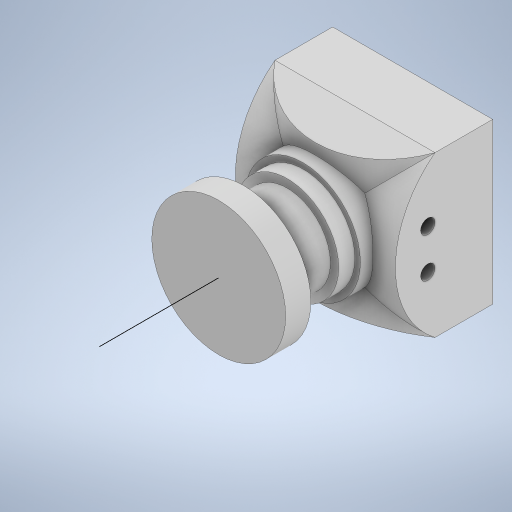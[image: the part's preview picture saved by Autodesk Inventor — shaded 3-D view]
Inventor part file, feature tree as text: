
AUTODESK INVENTOR PART (.ipt)
format: ipt  version: 2023 (Build 270158000, 158)  size: 368,640 bytes
history: native  units: in
note: dims shown in document units (in); Inventor stores cm internally (conversion verified against a paired STEP export)
features: sketch x12, extrude x9, projected_geometry x7, plane x2
ambient origin geometry x8: Origin, YZ Plane, XZ Plane, XY Plane, X Axis, Y Axis, Z Axis, Center Point
bodies: Solid1 (feature_tree)
feature tree (30):
  extrude  "Extrusion1"  Depth=0.874in
  extrude  "Extrusion2"  Depth=0.315in
  sketch  "Sketch3"  dims[d5=0.2854in d6=0.0in d9=0.2165in]
  extrude  "Extrusion4"  Depth=0.2165in
  extrude  "Extrusion5"  Depth=0.0886in
  extrude  "Extrusion6"  Depth=0.374in
  extrude  "Extrusion8"  Depth=0.0886in TaperAngle=0.0deg
  extrude  "Extrusion9"  Depth=0.2362in TaperAngle=0.0deg
  extrude  "Extrusion10"  Depth=0.1378in TaperAngle=0.0deg
  sketch  "Sketch12"  dims[d41=0.4409in]
  plane  "Work Plane2"
  extrude  "Extrusion12"  Depth=0.0394in
  plane  "Work Plane4"
  sketch  "Sketch18"  dims[d49=0.1083in d50=0.0787in d52=0.1083in d53=0.0787in d54=0.0in d55=0.0in d56=-0.437in]
  sketch  "Sketch1"  dims[d0=0.874in d1=0.874in]
  sketch  "Sketch2"  dims[d2=0.315in d3=0.0in d4=0.6299in]
  projected_geometry  "Projected Loop1"
  sketch  "Sketch5"  dims[d10=0.0886in d11=0.0in d12=0.2165in]
  projected_geometry  "Projected Loop3"
  sketch  "Sketch6"  dims[d13=0.0886in d14=0.0in d15=0.374in]
  projected_geometry  "Projected Loop4"
  sketch  "Sketch7"  dims[d16=0.0886in d17=0.0in d23=0.0886in d24=0.0in]
  projected_geometry  "Projected Loop5"
  sketch  "Sketch9"  dims[d25=0.0787in d26=0.2362in d27=0.0in]
  projected_geometry  "Projected Loop8"
  sketch  "Sketch10"  dims[d28=0.7307in d29=0.1378in d30=0.0in]
  projected_geometry  "Projected Loop9"
  sketch  "Sketch11"  dims[d31=1.063in d36=0.0394in]
  sketch  "Sketch17"  dims[d48=0.3543in]
  projected_geometry  "Projected Loop11"
